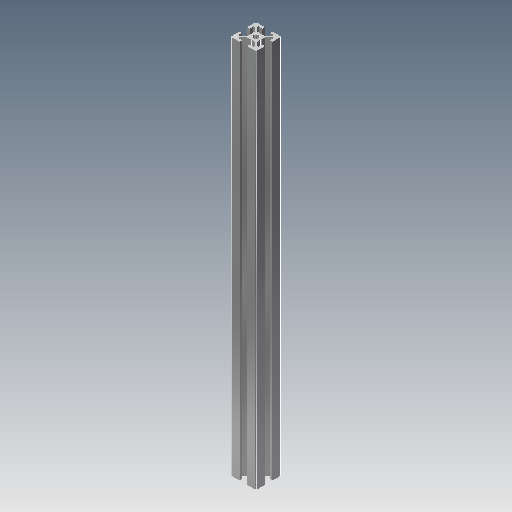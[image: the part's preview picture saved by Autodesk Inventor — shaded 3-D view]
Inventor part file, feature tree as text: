
AUTODESK INVENTOR PART (.ipt)
format: ipt  version: 2018.2 (Build 222227000, 227)  size: 160,768 bytes
history: native  units: mm
features: extrude x1, sketch x1
ambient origin geometry x8: Origin, YZ Plane, XZ Plane, XY Plane, X Axis, Y Axis, Z Axis, Center Point
bodies: Solid1 (feature_tree)
feature tree (2):
  extrude  "Extrusion1"  [1 undecoded]
  sketch  "Sketch1"  dims[d0=300.0mm d1=0.0mm]
note: 1 required parameter value undecoded (feature->parameter linkage not recoverable at this tier; creation-order binding heuristic only, values carry confidence <= 0.55)
